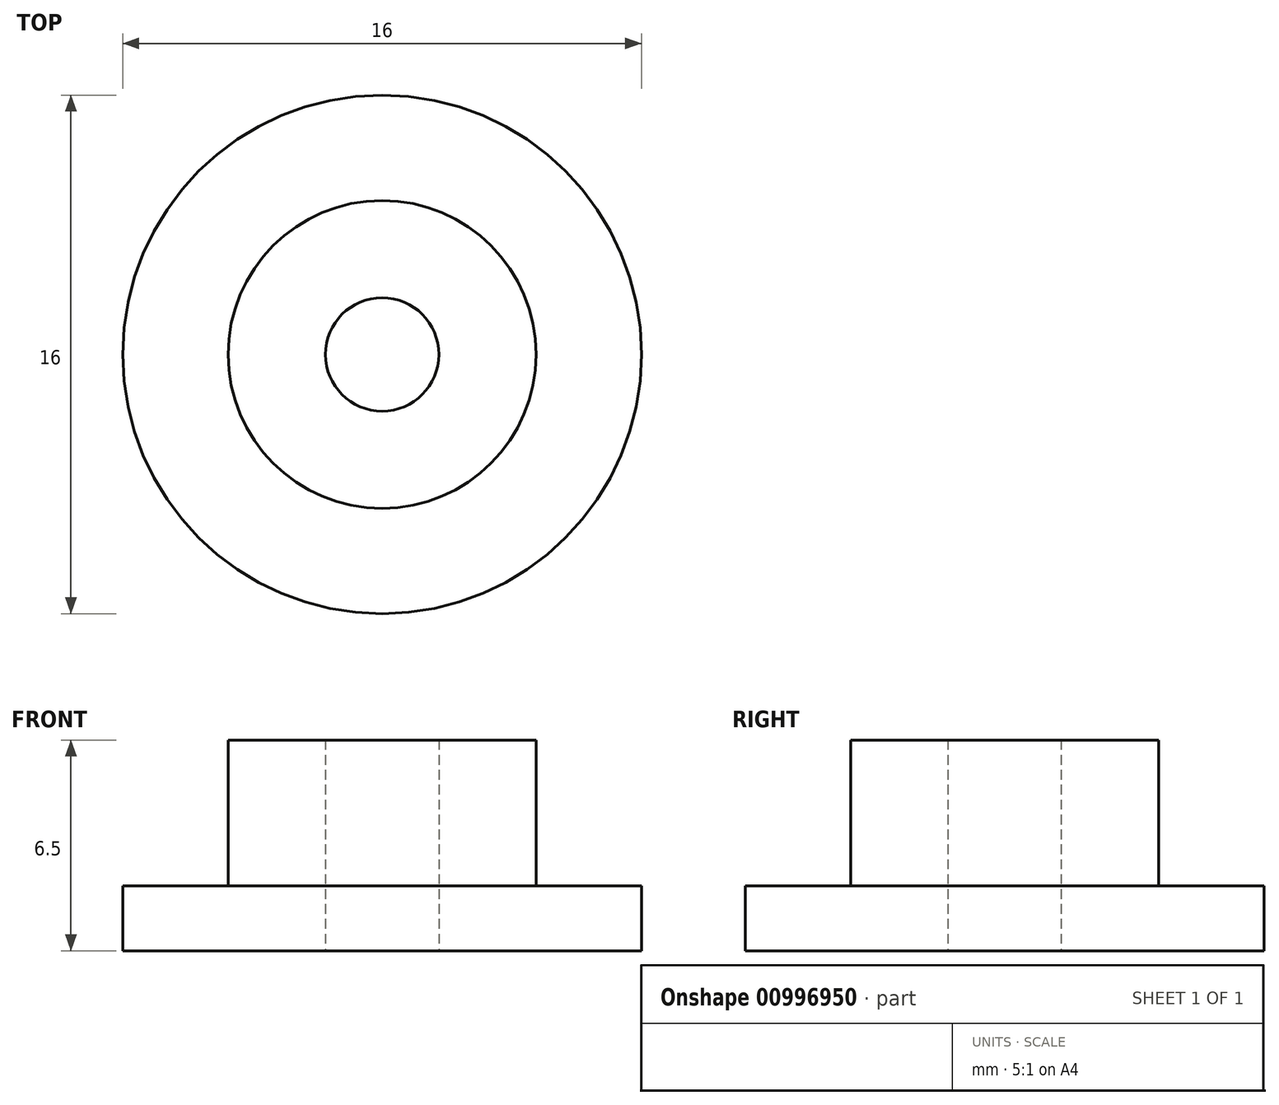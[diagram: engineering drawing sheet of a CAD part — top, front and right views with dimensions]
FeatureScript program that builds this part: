
annotation { "Feature Type Name" : "Feature", "Feature Type Description" : "" }
export const myFeature = defineFeature(function(context is Context, id is Id, definition is map)
    precondition{}
    {
        {
            var Q0;
            Q0=qCreatedBy(makeId("Top.planeOp"),FACE);
            var sketch = newSketch(context, id + "F0", { "sketchPlane" : qUnion([Q0])});
            skCircle(sketch, "E0", {"center": v(0, 0) * mm, "radius": 8 * mm});
            skCircle(sketch, "E1", {"center": v(0, 0) * mm, "radius": 1.75 * mm});
            skSolve(sketch);
        }
        {
            var Q0;
            Q0 = qSketchRegion(id + "F0", true);
            var Q1;
            Q1=makeQuery(id+"F0.imprint","IMPRINT",FACE,{"disambiguationData":[TD([[makeQuery(id+"F0.imprint","IMPRINT",EDGE,{"derivedFrom":sQuery(id+"F0.wireOp",EDGE,"E0")}),1.0]])]});
            extrude(context, id + "F1", {"entities" : qUnion([Q0, Q1]), "depth" : 2 * mm, "offsetDistance" : 25 * mm});
        }
        {
            var Q0;
            Q0=makeQuery(id+"F1.opExtrude","CAP_FACE",FACE,{"disambiguationData":[OSD([sQuery(id+"F0.wireOp",EDGE,"E0")])],"isStart":false});
            var sketch = newSketch(context, id + "F2", { "sketchPlane" : qUnion([Q0])});
            skCircle(sketch, "E2", {"center": v(0, 0) * mm, "radius": 4.75 * mm});
            skSolve(sketch);
        }
        {
            var Q0;
            Q0=makeQuery(id+"F2.imprint","IMPRINT",FACE,{"disambiguationData":[TD([[makeQuery(id+"F2.imprint","IMPRINT",EDGE,{"derivedFrom":sQuery(id+"F2.wireOp",EDGE,"E2")}),1.0]])]});
            extrude(context, id + "F3", {"entities" : qUnion([Q0]), "operationType" : NewBodyOperationType.ADD, "depth" : 4.5 * mm, "offsetDistance" : 25 * mm});
        }
    });
